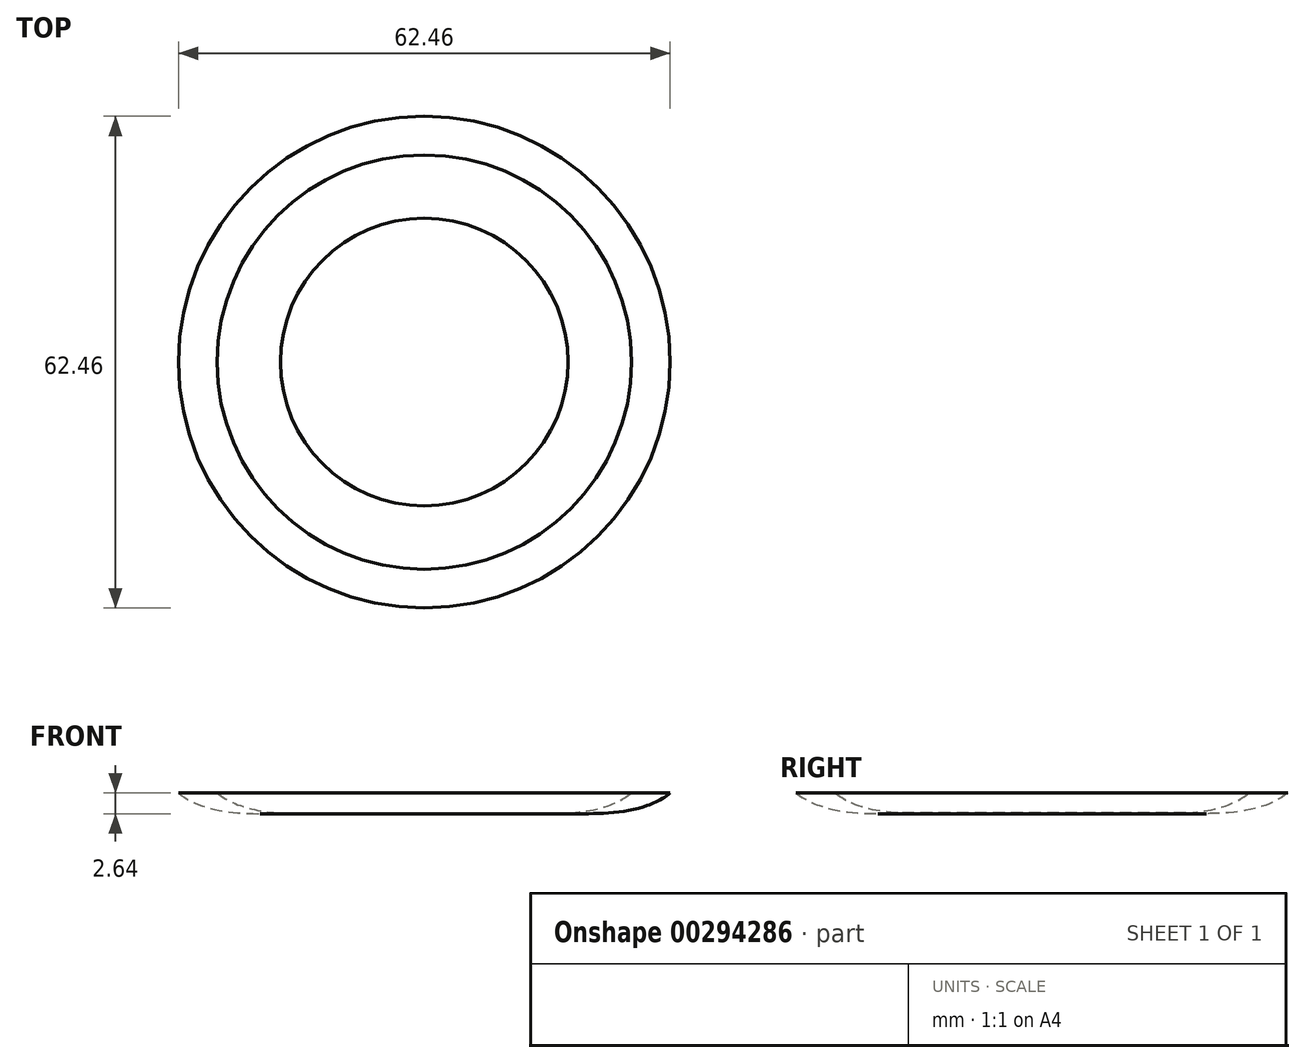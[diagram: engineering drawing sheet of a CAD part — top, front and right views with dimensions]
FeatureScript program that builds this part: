
annotation { "Feature Type Name" : "Feature", "Feature Type Description" : "" }
export const myFeature = defineFeature(function(context is Context, id is Id, definition is map)
    precondition{}
    {
        {
            var Q0;
            Q0=qCreatedBy(makeId("Front.planeOp"),FACE);
            var sketch = newSketch(context, id + "F0", { "sketchPlane" : qUnion([Q0])});
            skLineSegment(sketch, "E0.bottom", {"start": v(0, 0) * mm, "end": v(-31.23, 0) * mm});
            skLineSegment(sketch, "E0.top", {"start": v(0, 20) * mm, "end": v(-31.5, 20) * mm});
            skLineSegment(sketch, "E0.left", {"start": v(0, 0) * mm, "end": v(0, 20) * mm});
            skFitSpline(sketch, "E1", {"points": [v(-35, 20) * mm, v(-31.23, 0) * mm, v(0, 0) * mm], "startDerivative": vector(-2.3, -54.78) * mm, "endDerivative": vector(69.73, 12.39) * mm});
            skLineSegment(sketch, "E2", {"start": v(0, 20) * mm, "end": v(-30, 20) * mm});
            skFitSpline(sketch, "E3", {"points": [v(-30.09, 20) * mm, v(-26.32, 0) * mm, v(4.91, 0) * mm], "startDerivative": vector(-2.3, -54.78) * mm, "endDerivative": vector(69.73, 12.39) * mm});
            skLineSegment(sketch, "E4.bottom", {"start": v(-26.32, 0) * mm, "end": v(-26.07, 0) * mm});
            skLineSegment(sketch, "E4.right", {"start": v(-26.07, 0) * mm, "end": v(-26.07, 3.17) * mm});
            skLineSegment(sketch, "E5.left", {"start": v(-26.07, 0) * mm, "end": v(-26.07, 1) * mm});
            skLineSegment(sketch, "E6", {"start": v(-35, 20) * mm, "end": v(-33.5, 20) * mm});
            skLineSegment(sketch, "E7", {"start": v(-33.5, 20) * mm, "end": v(-33.5, 18) * mm});
            skLineSegment(sketch, "E8", {"start": v(-33.5, 18) * mm, "end": v(-31.5, 18) * mm});
            skLineSegment(sketch, "E9", {"start": v(-31.5, 18) * mm, "end": v(-31.5, 20) * mm});
            skLineSegment(sketch, "E10.trimOffspring", {"start": v(-33.5, 20) * mm, "end": v(-35, 20) * mm});
            skLineSegment(sketch, "E11", {"start": v(-26.07, 3.17) * mm, "end": v(-28.68, 3.17) * mm});
            skSolve(sketch);
        }
        {
            var Q0;
            {var subQ1=sQuery(id+"F0.wireOp",EDGE,"E1");Q0=makeQuery(id+"F0.imprint","IMPRINT",FACE,{"disambiguationData":[TD([[makeQuery(id+"F0.imprint","IMPRINT",EDGE,{"derivedFrom":subQ1}),1.0]])]});}
            var Q1;
            Q1=sQuery(id+"F0.wireOp",EDGE,"E0.left");
            revolve(context, id + "F1", {"entities" : qUnion([Q0]), "axis" : qUnion([Q1]), "revolveType" : RevolveType.FULL});
        }
    });
